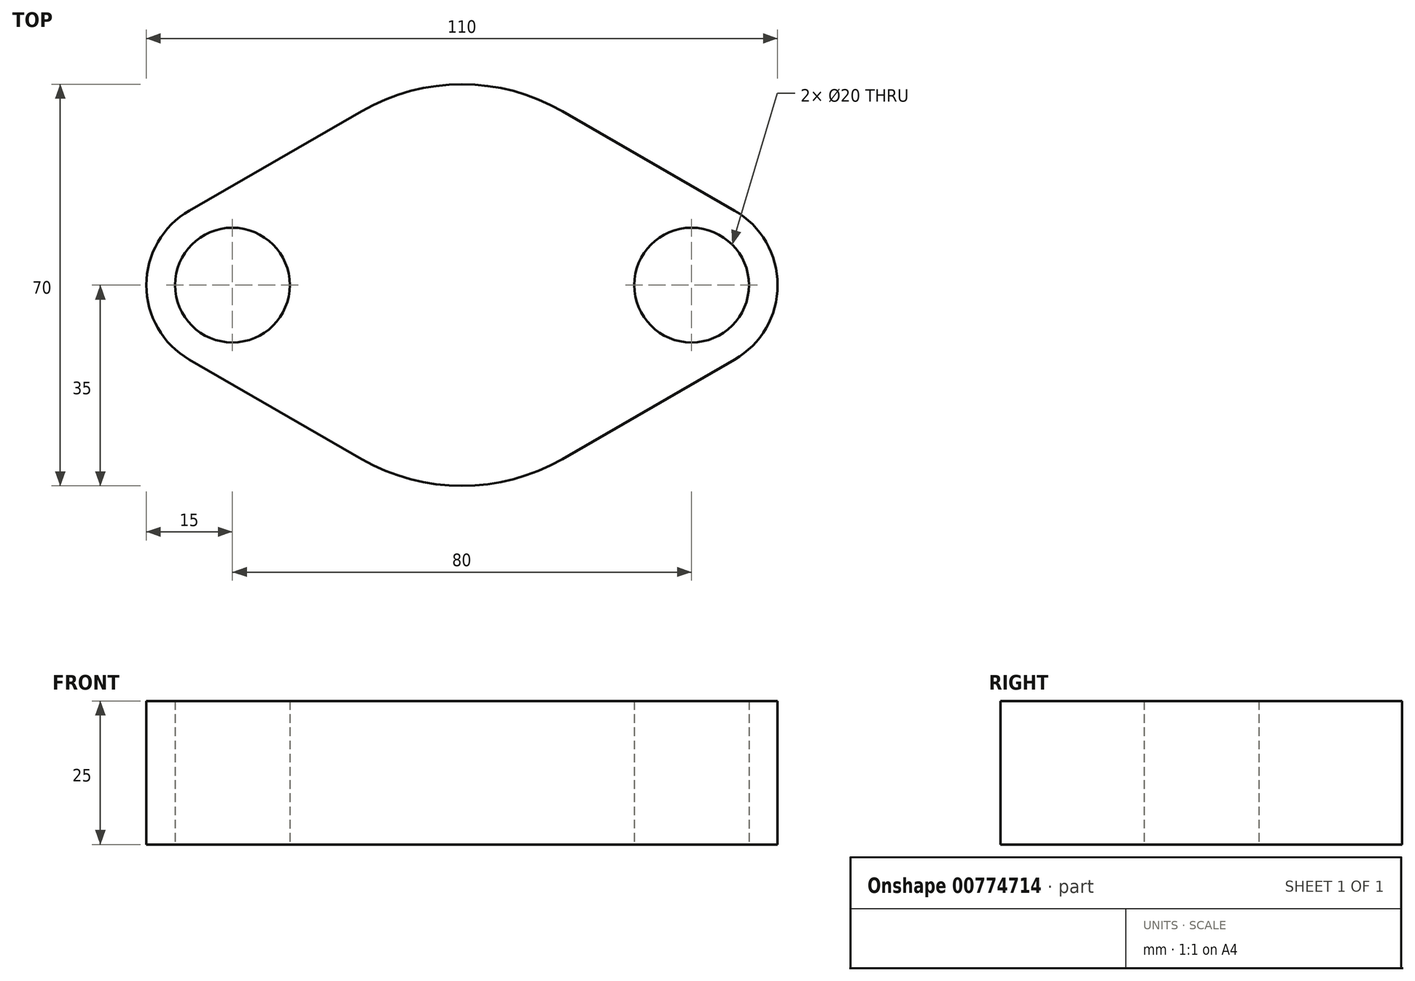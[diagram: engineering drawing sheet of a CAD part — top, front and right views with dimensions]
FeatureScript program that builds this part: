
annotation { "Feature Type Name" : "Feature", "Feature Type Description" : "" }
export const myFeature = defineFeature(function(context is Context, id is Id, definition is map)
    precondition{}
    {
        {
            var Q0;
            Q0=qCreatedBy(makeId("Top.planeOp"),FACE);
            var sketch = newSketch(context, id + "F0", { "sketchPlane" : qUnion([Q0])});
            skArc(sketch, "E0", {"start": v(-47.5, 13) * mm, "mid": v(-55, 0) * mm, "end": v(-47.5, -13) * mm});
            skArc(sketch, "E1", {"start": v(-17.5, -30.31) * mm, "mid": v(0, -35) * mm, "end": v(17.5, -30.31) * mm});
            skArc(sketch, "E2", {"start": v(47.5, -13) * mm, "mid": v(55, 0) * mm, "end": v(47.5, 13) * mm});
            skLineSegment(sketch, "E3", {"start": v(-17.5, -30.31) * mm, "end": v(-47.5, -13) * mm});
            skLineSegment(sketch, "E4", {"start": v(17.5, -30.31) * mm, "end": v(47.5, -13) * mm});
            skLineSegment(sketch, "E5", {"start": v(-47.5, 13) * mm, "end": v(-17.5, 30.31) * mm});
            skLineSegment(sketch, "E6", {"start": v(47.5, 13) * mm, "end": v(17.5, 30.31) * mm});
            skArc(sketch, "E7.trimOffspring", {"start": v(17.5, 30.31) * mm, "mid": v(0, 35) * mm, "end": v(-17.5, 30.31) * mm});
            skSolve(sketch);
        }
        {
            var Q0;
            Q0=makeQuery(id+"F0.imprint","IMPRINT",FACE,{"disambiguationData":[TD([[makeQuery(id+"F0.imprint","IMPRINT",EDGE,{"derivedFrom":sQuery(id+"F0.wireOp",EDGE,"E0")}),1.0]])]});
            var sketch = newSketch(context, id + "F1", { "sketchPlane" : qUnion([Q0])});
            skCircle(sketch, "E8", {"center": v(-40, 0) * mm, "radius": 10 * mm});
            skCircle(sketch, "E9", {"center": v(40, 0) * mm, "radius": 10 * mm});
            skSolve(sketch);
        }
        {
            var Q0;
            Q0 = qSketchRegion(id + "F0", true);
            extrude(context, id + "F2", {"entities" : qUnion([Q0]), "depth" : 25 * mm, "offsetDistance" : 25 * mm});
        }
        {
            var Q0;
            Q0=makeQuery(id+"F1.imprint","IMPRINT",FACE,{"disambiguationData":[TD([[makeQuery(id+"F1.imprint","IMPRINT",EDGE,{"derivedFrom":sQuery(id+"F1.wireOp",EDGE,"E9")}),1.0]])]});
            var Q1;
            Q1=makeQuery(id+"F1.imprint","IMPRINT",FACE,{"disambiguationData":[TD([[makeQuery(id+"F1.imprint","IMPRINT",EDGE,{"derivedFrom":sQuery(id+"F1.wireOp",EDGE,"E8")}),1.0]])]});
            extrude(context, id + "F3", {"entities" : qUnion([Q0, Q1]), "operationType" : NewBodyOperationType.REMOVE, "depth" : 25 * mm, "offsetDistance" : 25 * mm});
        }
    });
